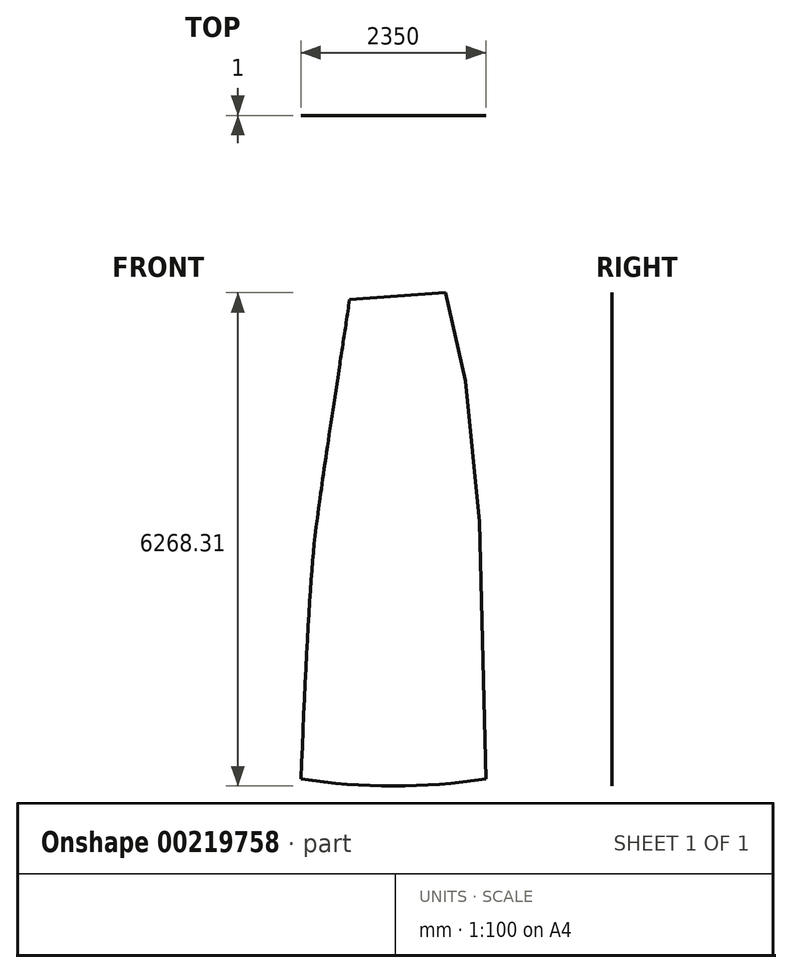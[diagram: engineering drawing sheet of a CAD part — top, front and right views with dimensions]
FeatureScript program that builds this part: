
annotation { "Feature Type Name" : "Feature", "Feature Type Description" : "" }
export const myFeature = defineFeature(function(context is Context, id is Id, definition is map)
    precondition{}
    {
        {
            var Q0;
            Q0=qCreatedBy(makeId("Front.planeOp"),FACE);
            var sketch = newSketch(context, id + "F0", { "sketchPlane" : qUnion([Q0])});
            skLineSegment(sketch, "E0", {"start": v(0, 0) * mm, "end": v(2350, 0) * mm});
            skLineSegment(sketch, "E1", {"start": v(0, 0) * mm, "end": v(618.72, 6088.64) * mm});
            skLineSegment(sketch, "E2", {"start": v(618.72, 6088.64) * mm, "end": v(2350, 0) * mm});
            skLineSegment(sketch, "E3", {"start": v(618.72, 6088.64) * mm, "end": v(1840.44, 6178.3) * mm});
            skLineSegment(sketch, "E4", {"start": v(1840.44, 6178.3) * mm, "end": v(2350, 0) * mm});
            skSolve(sketch);
        }
        {
            var Q0;
            Q0=makeQuery(id+"F0.imprint","IMPRINT",FACE,{"disambiguationData":[TD([[makeQuery(id+"F0.imprint","IMPRINT",EDGE,{"derivedFrom":sQuery(id+"F0.wireOp",EDGE,"E0")}),1.0]])]});
            var sketch = newSketch(context, id + "F1", { "sketchPlane" : qUnion([Q0])});
            skLineSegment(sketch, "E5", {"start": v(618.72, 6088.64) * mm, "end": v(1840.44, 6178.3) * mm});
            skLineSegment(sketch, "E6", {"start": v(1840.44, 6178.3) * mm, "end": v(2350, 0) * mm});
            skLineSegment(sketch, "E7", {"start": v(618.72, 6088.64) * mm, "end": v(2350, 0) * mm});
            skSolve(sketch);
        }
        {
            var Q0;
            Q0=makeQuery(id+"F0.imprint","IMPRINT",FACE,{"disambiguationData":[TD([[makeQuery(id+"F0.imprint","IMPRINT",EDGE,{"derivedFrom":sQuery(id+"F0.wireOp",EDGE,"E0")}),1.0]])]});
            var sketch = newSketch(context, id + "F2", { "sketchPlane" : qUnion([Q0])});
            skArc(sketch, "E8", {"start": v(0, 0) * mm, "mid": v(1175, -90) * mm, "end": v(2350, 0) * mm});
            skLineSegment(sketch, "E9", {"start": v(620.2, 6088.5) * mm, "end": v(1840.44, 6178.3) * mm});
            skFitSpline(sketch, "E10", {"points": [v(0, 0) * mm, v(127.67, 2496.74) * mm, v(233.1, 3492.23) * mm, v(620.2, 6088.5) * mm], "startDerivative": vector(340.46, 7570.42) * mm, "endDerivative": vector(1177.6, 7705.28) * mm});
            skPoint(sketch, "E11", {"position": v(1484.36, 3044.32) * mm});
            skLineSegment(sketch, "E12", {"start": v(1484.36, 3044.32) * mm, "end": v(3058.7, 3491.98) * mm});
            skLineSegment(sketch, "E13", {"start": v(2271.53, 3268.15) * mm, "end": v(243.3, 3566.19) * mm});
            skLineSegment(sketch, "E14", {"start": v(620.2, 6088.5) * mm, "end": v(2271.53, 3268.15) * mm});
            skPoint(sketch, "E15", {"position": v(1445.86, 4678.32) * mm});
            skLineSegment(sketch, "E16", {"start": v(2091.07, 5056.1) * mm, "end": v(495.54, 5271.52) * mm});
            skLineSegment(sketch, "E17", {"start": v(1445.86, 4678.32) * mm, "end": v(2308.68, 5183.5) * mm});
            skLineSegment(sketch, "E18", {"start": v(2350, 0) * mm, "end": v(2271.53, 3268.15) * mm});
            skLineSegment(sketch, "E19", {"start": v(2091.07, 5056.1) * mm, "end": v(2271.53, 3268.15) * mm});
            skLineSegment(sketch, "E20", {"start": v(2091.07, 5056.1) * mm, "end": v(1840.44, 6178.3) * mm});
            skSolve(sketch);
        }
        {
            var Q0;
            Q0=qSketchRegion(id+"F2",true);
            extrude(context, id + "F3", {"entities" : qUnion([Q0]), "depth" : 1 * mm});
        }
    });
